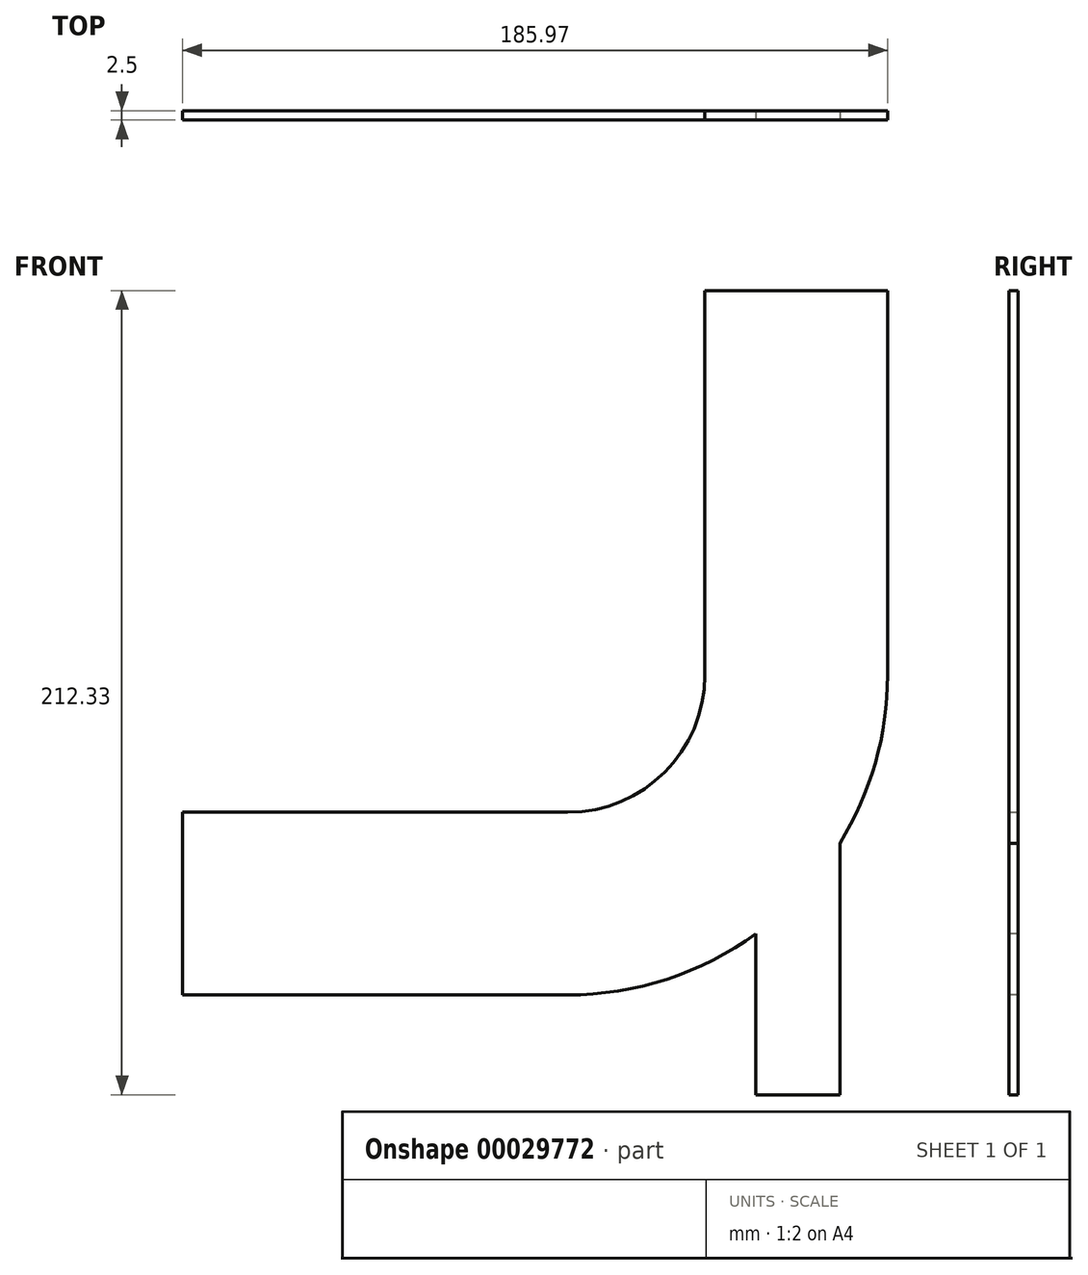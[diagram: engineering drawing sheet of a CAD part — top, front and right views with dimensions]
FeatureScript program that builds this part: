
annotation { "Feature Type Name" : "Feature", "Feature Type Description" : "" }
export const myFeature = defineFeature(function(context is Context, id is Id, definition is map)
    precondition{}
    {
        {
            var Q0;
            Q0=qCreatedBy(makeId("Right.planeOp"),FACE);
            var sketch = newSketch(context, id + "F0", { "sketchPlane" : qUnion([Q0])});
            skLineSegment(sketch, "E0.bottom", {"start": v(2.5, 24.18) * mm, "end": v(2.5, 24.18) * mm});
            skLineSegment(sketch, "E1", {"start": v(2.5, -24.05) * mm, "end": v(2.5, 24.18) * mm});
            skLineSegment(sketch, "E2", {"start": v(2.5, -24.05) * mm, "end": v(0, -24.05) * mm});
            skLineSegment(sketch, "E3", {"start": v(0, -24.05) * mm, "end": v(0, 24.18) * mm});
            skLineSegment(sketch, "E4", {"start": v(0, 24.18) * mm, "end": v(2.5, 24.18) * mm});
            skSolve(sketch);
        }
        {
            var Q0;
            Q0=qCreatedBy(makeId("Front.planeOp"),FACE);
            var sketch = newSketch(context, id + "F1", { "sketchPlane" : qUnion([Q0])});
            skLineSegment(sketch, "E5", {"start": v(0, 0) * mm, "end": v(101.6, 0) * mm});
            skLineSegment(sketch, "E6", {"start": v(101.6, 0) * mm, "end": v(101.6, 60.33) * mm, "construction": true});
            skArc(sketch, "E7", {"start": v(101.6, 0) * mm, "mid": v(144.26, 17.67) * mm, "end": v(161.92, 60.32) * mm});
            skLineSegment(sketch, "E8", {"start": v(101.6, 60.32) * mm, "end": v(188.95, 60.32) * mm, "construction": true});
            skLineSegment(sketch, "E9", {"start": v(161.92, 60.32) * mm, "end": v(161.92, 161.92) * mm});
            skSolve(sketch);
        }
        {
            var Q0;
            Q0 = qSketchRegion(id + "F0", true);
            var Q1;
            Q1 = qConstructionFilter(qBodyType(qCreatedBy(id + "F1" ,EDGE), BodyType.WIRE), ConstructionObject.NO);
            sweep(context, id + "F2", {"profiles" : qUnion([Q0]), "path" : qUnion([Q1])});
        }
        {
            var Q0;
            Q0=qCreatedBy(makeId("Top.planeOp"),FACE);
            cPlane(context, id + "F3", {"entities" : qUnion([Q0]), "cplaneType" : CPlaneType.OFFSET, "offset" : 25.4 * mm, "oppositeDirection" : true, "width" : 150 * mm, "height" : 150 * mm});
        }
        {
            var Q0;
            Q0=qCreatedBy(id+"F3.planeOp",FACE);
            var sketch = newSketch(context, id + "F4", { "sketchPlane" : qUnion([Q0])});
            skLineSegment(sketch, "E10", {"start": v(151.25, 0) * mm, "end": v(173.37, 0) * mm});
            skLineSegment(sketch, "E11", {"start": v(151.25, 0) * mm, "end": v(151.25, 2.5) * mm});
            skLineSegment(sketch, "E12", {"start": v(151.25, 2.5) * mm, "end": v(173.37, 2.5) * mm});
            skLineSegment(sketch, "E13", {"start": v(173.37, 2.5) * mm, "end": v(173.37, 0) * mm});
            skSolve(sketch);
        }
        {
            var Q0;
            Q0 = qSketchRegion(id + "F4", true);
            extrude(context, id + "F5", {"entities" : qUnion([Q0]), "operationType" : NewBodyOperationType.ADD, "endBound" : BoundingType.UP_TO_NEXT, "depth" : 25 * mm, "hasSecondDirection" : true, "secondDirectionOppositeDirection" : true, "secondDirectionDepth" : 25 * mm});
        }
    });
